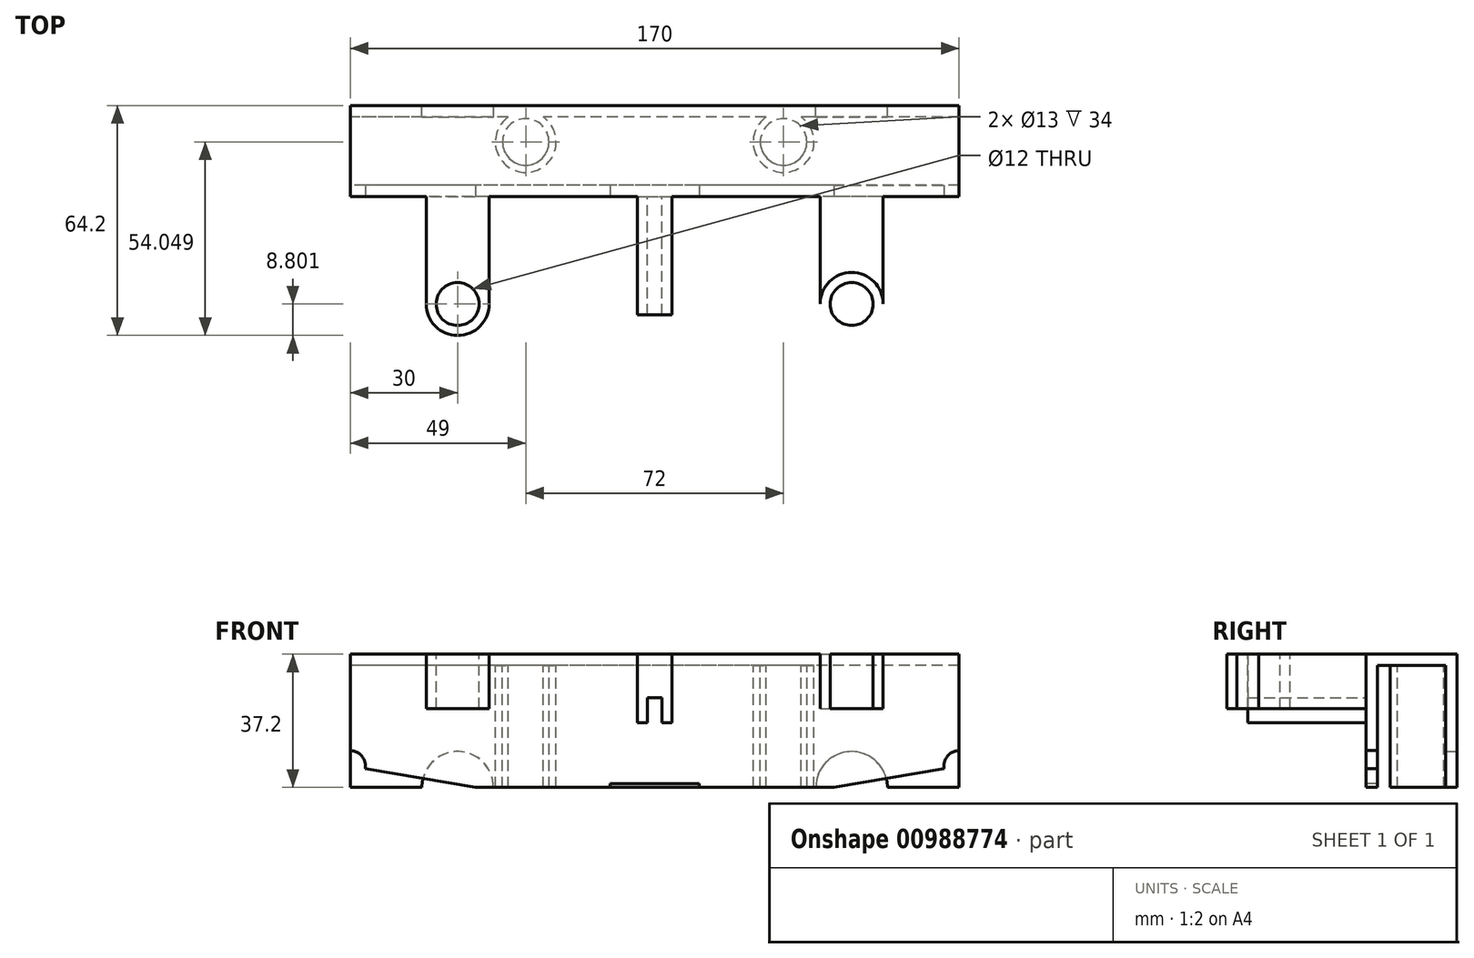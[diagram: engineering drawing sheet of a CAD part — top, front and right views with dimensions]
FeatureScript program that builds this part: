
annotation { "Feature Type Name" : "Feature", "Feature Type Description" : "" }
export const myFeature = defineFeature(function(context is Context, id is Id, definition is map)
    precondition{}
    {
        {
            var Q0;
            Q0=qCreatedBy(makeId("Right.planeOp"),FACE);
            var sketch = newSketch(context, id + "F0", { "sketchPlane" : qUnion([Q0])});
            skLineSegment(sketch, "E0", {"start": v(2.75, 37.2) * mm, "end": v(-22.65, 37.2) * mm});
            skLineSegment(sketch, "E1", {"start": v(-22.65, 37.2) * mm, "end": v(-22.65, 0) * mm});
            skLineSegment(sketch, "E2", {"start": v(-22.65, 0) * mm, "end": v(-19.45, 0) * mm});
            skLineSegment(sketch, "E3", {"start": v(-19.45, 0) * mm, "end": v(-19.45, 34) * mm});
            skLineSegment(sketch, "E4", {"start": v(-19.45, 34) * mm, "end": v(-0.45, 34) * mm});
            skLineSegment(sketch, "E5", {"start": v(-0.45, 34) * mm, "end": v(-0.45, 0) * mm});
            skLineSegment(sketch, "E6", {"start": v(-0.45, 0) * mm, "end": v(2.75, 0) * mm});
            skLineSegment(sketch, "E7", {"start": v(2.75, 0) * mm, "end": v(2.75, 37.2) * mm});
            skSolve(sketch);
        }
        {
            var Q0;
            Q0=makeQuery(id+"F0.imprint","IMPRINT",FACE,{"disambiguationData":[TD([[makeQuery(id+"F0.imprint","IMPRINT",EDGE,{"derivedFrom":sQuery(id+"F0.wireOp",EDGE,"E0")}),1.0]])]});
            extrude(context, id + "F1", {"entities" : qUnion([Q0]), "endBound" : BoundingType.SYMMETRIC, "depth" : 170 * mm, "offsetDistance" : 25 * mm});
        }
        {
            var Q0;
            Q0=makeQuery(id+"F1.opExtrude","SWEPT_FACE",FACE,{"disambiguationData":[OSD([sQuery(id+"F0.wireOp",EDGE,"E7")])]});
            var sketch = newSketch(context, id + "F2", { "sketchPlane" : qUnion([Q0])});
            skLineSegment(sketch, "E8", {"start": v(-55, 0) * mm, "end": v(55, 0) * mm, "construction": true});
            skPoint(sketch, "E9", {"position": v(0, 0) * mm});
            skArc(sketch, "E10", {"start": v(-45, 0) * mm, "mid": v(-55, 10) * mm, "end": v(-65, 0) * mm});
            skArc(sketch, "E11", {"start": v(65, 0) * mm, "mid": v(55, 10) * mm, "end": v(45, 0) * mm});
            skLineSegment(sketch, "E12", {"start": v(-65, 0) * mm, "end": v(-45, 0) * mm});
            skLineSegment(sketch, "E13", {"start": v(45, 0) * mm, "end": v(65, 0) * mm});
            skSolve(sketch);
        }
        {
            var Q0;
            Q0=makeQuery(id+"F2.imprint","IMPRINT",FACE,{"disambiguationData":[TD([[makeQuery(id+"F2.imprint","IMPRINT",EDGE,{"derivedFrom":sQuery(id+"F2.wireOp",EDGE,"E10")}),1.0]])]});
            var Q1;
            Q1=makeQuery(id+"F2.imprint","IMPRINT",FACE,{"disambiguationData":[TD([[makeQuery(id+"F2.imprint","IMPRINT",EDGE,{"derivedFrom":sQuery(id+"F2.wireOp",EDGE,"E11")}),1.0]])]});
            var Q2;
            Q2=makeQuery(id+"F1.opExtrude","SWEPT_FACE",FACE,{"disambiguationData":[OSD([sQuery(id+"F0.wireOp",EDGE,"E5")])]});
            extrude(context, id + "F3", {"entities" : qUnion([Q0, Q1]), "operationType" : NewBodyOperationType.REMOVE, "endBound" : BoundingType.UP_TO_SURFACE, "oppositeDirection" : true, "depth" : 25 * mm, "endBoundEntityFace" : qUnion([Q2]), "offsetDistance" : 25 * mm});
        }
        {
            var Q0;
            Q0=makeQuery(id+"F1.opExtrude","SWEPT_FACE",FACE,{"disambiguationData":[OSD([sQuery(id+"F0.wireOp",EDGE,"E1")])]});
            var sketch = newSketch(context, id + "F4", { "sketchPlane" : qUnion([Q0])});
            skPoint(sketch, "E14.0", {"position": v(0, 34) * mm});
            skLineSegment(sketch, "E15", {"start": v(-85, 6) * mm, "end": v(-50, 0) * mm});
            skLineSegment(sketch, "E16", {"start": v(-50, 0) * mm, "end": v(-85, 0) * mm});
            skLineSegment(sketch, "E17", {"start": v(-85, 0) * mm, "end": v(-85, 6) * mm});
            skLineSegment(sketch, "E18.MirrorCS", {"start": v(85, 6) * mm, "end": v(50, 0) * mm});
            skLineSegment(sketch, "E19.MirrorCS", {"start": v(50, 0) * mm, "end": v(85, 0) * mm});
            skLineSegment(sketch, "E20.MirrorCS", {"start": v(85, 0) * mm, "end": v(85, 6) * mm});
            skLineSegment(sketch, "E21", {"start": v(-12.5, 1) * mm, "end": v(12.5, 1) * mm});
            skPoint(sketch, "E22", {"position": v(0, 1) * mm});
            skLineSegment(sketch, "E23", {"start": v(-12.5, 1) * mm, "end": v(-12.5, 0) * mm});
            skLineSegment(sketch, "E24", {"start": v(-12.5, 0) * mm, "end": v(12.5, 0) * mm});
            skLineSegment(sketch, "E25", {"start": v(12.5, 0) * mm, "end": v(12.5, 1) * mm});
            skLineSegment(sketch, "E26", {"start": v(-82, 9) * mm, "end": v(82, 9) * mm, "construction": true});
            skPoint(sketch, "E27", {"position": v(0, 9) * mm});
            skArc(sketch, "E28", {"start": v(85, 10.24) * mm, "mid": v(81.76, 8.73) * mm, "end": v(80.82, 5.28) * mm});
            skLineSegment(sketch, "E29", {"start": v(85, 6) * mm, "end": v(85, 10.24) * mm});
            skArc(sketch, "E30", {"start": v(-80.82, 5.28) * mm, "mid": v(-81.76, 8.73) * mm, "end": v(-85, 10.24) * mm});
            skLineSegment(sketch, "E31", {"start": v(-85, 10.24) * mm, "end": v(-85, 6) * mm});
            skSolve(sketch);
        }
        {
            var Q0;
            Q0=makeQuery(id+"F4.imprint","IMPRINT",FACE,{"disambiguationData":[TD([[makeQuery(id+"F4.imprint","IMPRINT",EDGE,{"derivedFrom":sQuery(id+"F4.wireOp",EDGE,"E15")}),-1.0]])]});
            var Q1;
            Q1=makeQuery(id+"F4.imprint","IMPRINT",FACE,{"disambiguationData":[TD([[makeQuery(id+"F4.imprint","IMPRINT",EDGE,{"derivedFrom":sQuery(id+"F4.wireOp",EDGE,"E18.MirrorCS")}),1.0]])]});
            var Q2;
            Q2=makeQuery(id+"F4.imprint","IMPRINT",FACE,{"disambiguationData":[TD([[makeQuery(id+"F4.imprint","IMPRINT",EDGE,{"derivedFrom":sQuery(id+"F4.wireOp",EDGE,"E21")}),-1.0]])]});
            var Q3;
            {var subQ2=sQuery(id+"F4.wireOp",EDGE,"E30");Q3=makeQuery(id+"F4.imprint","IMPRINT",FACE,{"disambiguationData":[TD([[makeQuery(id+"F4.imprint","IMPRINT",EDGE,{"derivedFrom":subQ2}),1.0]])]});}
            var Q4;
            {var subQ2=sQuery(id+"F4.wireOp",EDGE,"E28");Q4=makeQuery(id+"F4.imprint","IMPRINT",FACE,{"disambiguationData":[TD([[makeQuery(id+"F4.imprint","IMPRINT",EDGE,{"derivedFrom":subQ2}),1.0]])]});}
            var Q5;
            Q5=makeQuery(id+"F1.opExtrude","SWEPT_FACE",FACE,{"disambiguationData":[OSD([sQuery(id+"F0.wireOp",EDGE,"E3")])]});
            extrude(context, id + "F5", {"entities" : qUnion([Q0, Q1, Q2, Q3, Q4]), "operationType" : NewBodyOperationType.REMOVE, "endBound" : BoundingType.UP_TO_SURFACE, "oppositeDirection" : true, "depth" : 25 * mm, "endBoundEntityFace" : qUnion([Q5]), "offsetDistance" : 25 * mm});
        }
        {
            var Q0;
            Q0=makeQuery(id+"F1.opExtrude","SWEPT_FACE",FACE,{"disambiguationData":[OSD([sQuery(id+"F0.wireOp",EDGE,"E4")])]});
            var sketch = newSketch(context, id + "F6", { "sketchPlane" : qUnion([Q0])});
            skLineSegment(sketch, "E32", {"start": v(-36, 7.4) * mm, "end": v(36, 7.4) * mm, "construction": true});
            skPoint(sketch, "E33", {"position": v(0, 7.4) * mm});
            skCircle(sketch, "E34", {"center": v(-36, 7.4) * mm, "radius": 6.5 * mm});
            skCircle(sketch, "E35", {"center": v(36, 7.4) * mm, "radius": 6.5 * mm});
            skArc(sketch, "E36.0", {"start": v(-31.1, 0.45) * mm, "mid": v(-36, 15.9) * mm, "end": v(-40.9, 0.45) * mm});
            skArc(sketch, "E37.0", {"start": v(40.9, 0.45) * mm, "mid": v(36, 15.9) * mm, "end": v(31.1, 0.45) * mm});
            skLineSegment(sketch, "E38", {"start": v(-40.9, 0.45) * mm, "end": v(-31.1, 0.45) * mm});
            skLineSegment(sketch, "E39", {"start": v(31.1, 0.45) * mm, "end": v(40.9, 0.45) * mm});
            skSolve(sketch);
        }
        {
            var Q0;
            Q0=makeQuery(id+"F6.imprint","IMPRINT",FACE,{"disambiguationData":[TD([[makeQuery(id+"F6.imprint","IMPRINT",EDGE,{"derivedFrom":sQuery(id+"F6.wireOp",EDGE,"E35")}),-1.0]])]});
            var Q1;
            Q1=makeQuery(id+"F6.imprint","IMPRINT",FACE,{"disambiguationData":[TD([[makeQuery(id+"F6.imprint","IMPRINT",EDGE,{"derivedFrom":sQuery(id+"F6.wireOp",EDGE,"E34")}),-1.0]])]});
            var Q2;
            Q2=makeQuery(id+"F3.boolean.opBoolean","SPLIT",FACE,{"disambiguationData":[TD([makeQuery(id+"F1.opExtrude","SWEPT_FACE",FACE,{"disambiguationData":[OSD([sQuery(id+"F0.wireOp",EDGE,"E5")])]}),makeQuery(id+"F1.opExtrude","SWEPT_FACE",FACE,{"disambiguationData":[OSD([sQuery(id+"F0.wireOp",EDGE,"E7")])]}),makeQuery(id+"F3.opExtrude","SWEPT_FACE",FACE,{"disambiguationData":[OSD([sQuery(id+"F2.wireOp",EDGE,"E10")])]}),makeQuery(id+"F3.opExtrude","SWEPT_FACE",FACE,{"disambiguationData":[OSD([sQuery(id+"F2.wireOp",EDGE,"E11")])]})])],"derivedFrom":makeQuery(id+"F1.opExtrude","SWEPT_FACE",FACE,{"disambiguationData":[OSD([sQuery(id+"F0.wireOp",EDGE,"E6")])]})});
            extrude(context, id + "F7", {"entities" : qUnion([Q0, Q1]), "operationType" : NewBodyOperationType.ADD, "endBound" : BoundingType.UP_TO_SURFACE, "depth" : 25 * mm, "endBoundEntityFace" : qUnion([Q2]), "offsetDistance" : 25 * mm});
        }
        {
            var Q0;
            Q0=makeQuery(id+"F1.opExtrude","SWEPT_FACE",FACE,{"disambiguationData":[OSD([sQuery(id+"F0.wireOp",EDGE,"E1")])]});
            var sketch = newSketch(context, id + "F8", { "sketchPlane" : qUnion([Q0])});
            skPoint(sketch, "E40", {"position": v(0, 25) * mm});
            skLineSegment(sketch, "E41", {"start": v(-2, 25) * mm, "end": v(2, 25) * mm});
            skLineSegment(sketch, "E42", {"start": v(-2, 25) * mm, "end": v(-2, 18) * mm});
            skLineSegment(sketch, "E43", {"start": v(2, 18) * mm, "end": v(2, 25) * mm});
            skLineSegment(sketch, "E44", {"start": v(2, 18) * mm, "end": v(4.8, 18) * mm});
            skLineSegment(sketch, "E45", {"start": v(4.8, 18) * mm, "end": v(4.8, 27.8) * mm});
            skLineSegment(sketch, "E46", {"start": v(4.8, 27.8) * mm, "end": v(-4.8, 27.8) * mm});
            skLineSegment(sketch, "E47", {"start": v(-4.8, 27.8) * mm, "end": v(-4.8, 18) * mm});
            skLineSegment(sketch, "E48", {"start": v(-4.8, 18) * mm, "end": v(-2, 18) * mm});
            skSolve(sketch);
        }
        {
            var Q0;
            Q0=makeQuery(id+"F8.imprint","IMPRINT",FACE,{"disambiguationData":[TD([[makeQuery(id+"F8.imprint","IMPRINT",EDGE,{"derivedFrom":sQuery(id+"F8.wireOp",EDGE,"E41")}),1.0]])]});
            extrude(context, id + "F9", {"entities" : qUnion([Q0]), "operationType" : NewBodyOperationType.ADD, "depth" : 33 * mm, "offsetDistance" : 25 * mm});
        }
        {
            var Q0;
            Q0=makeQuery(id+"F5.boolean.opBoolean","SPLIT",FACE,{"disambiguationData":[TD([makeQuery(id+"F5.opExtrude","SWEPT_FACE",FACE,{"disambiguationData":[OSD([sQuery(id+"F4.wireOp",EDGE,"E15")])]})])],"derivedFrom":makeQuery(id+"F1.opExtrude","SWEPT_FACE",FACE,{"disambiguationData":[OSD([sQuery(id+"F0.wireOp",EDGE,"E2")])]})});
            cPlane(context, id + "F10", {"entities" : qUnion([Q0]), "cplaneType" : CPlaneType.OFFSET, "offset" : 27 * mm, "oppositeDirection" : true, "width" : 150 * mm, "height" : 150 * mm});
        }
        {
            var Q0;
            Q0=qCreatedBy(id+"F10.planeOp",FACE);
            var sketch = newSketch(context, id + "F11", { "sketchPlane" : qUnion([Q0])});
            skPoint(sketch, "E49.0", {"position": v(-55, 52.65) * mm});
            skCircle(sketch, "E50", {"center": v(-55, 52.65) * mm, "radius": 6 * mm});
            skLineSegment(sketch, "E51.0", {"start": v(85, 22.65) * mm, "end": v(-85, 22.65) * mm, "construction": true});
            skCircle(sketch, "E52.0", {"center": v(-55, 52.65) * mm, "radius": 8.8 * mm});
            skLineSegment(sketch, "E53", {"start": v(-46.2, 52.65) * mm, "end": v(-46.2, 22.65) * mm});
            skLineSegment(sketch, "E54", {"start": v(-46.2, 22.65) * mm, "end": v(-63.8, 22.65) * mm});
            skLineSegment(sketch, "E55", {"start": v(-63.8, 22.65) * mm, "end": v(-63.8, 52.65) * mm});
            skCircle(sketch, "E56.MirrorC", {"center": v(55, 52.65) * mm, "radius": 8.8 * mm});
            skCircle(sketch, "E57.MirrorC", {"center": v(55, 52.65) * mm, "radius": 6 * mm});
            skLineSegment(sketch, "E58.MirrorCS", {"start": v(46.2, 52.65) * mm, "end": v(46.2, 22.65) * mm});
            skLineSegment(sketch, "E59.MirrorCS", {"start": v(63.8, 22.65) * mm, "end": v(63.8, 52.65) * mm});
            skLineSegment(sketch, "E60", {"start": v(63.8, 22.65) * mm, "end": v(46.2, 22.65) * mm});
            skSolve(sketch);
        }
        {
            var Q0;
            {var subQ0=sQuery(id+"F11.wireOp",EDGE,"E53");Q0=makeQuery(id+"F11.imprint","IMPRINT",FACE,{"disambiguationData":[TD([[makeQuery(id+"F11.imprint","IMPRINT",EDGE,{"derivedFrom":subQ0}),-1.0]])]});}
            var Q1;
            Q1=makeQuery(id+"F11.imprint","IMPRINT",FACE,{"disambiguationData":[TD([[makeQuery(id+"F11.imprint","IMPRINT",EDGE,{"derivedFrom":sQuery(id+"F11.wireOp",EDGE,"E50")}),-1.0]])]});
            var Q2;
            {var subQ0=sQuery(id+"F11.wireOp",EDGE,"E58.MirrorCS");Q2=makeQuery(id+"F11.imprint","IMPRINT",FACE,{"disambiguationData":[TD([[makeQuery(id+"F11.imprint","IMPRINT",EDGE,{"derivedFrom":subQ0}),1.0]])]});}
            var Q3;
            Q3=makeQuery(id+"F11.imprint","IMPRINT",FACE,{"disambiguationData":[TD([[makeQuery(id+"F11.imprint","IMPRINT",EDGE,{"derivedFrom":sQuery(id+"F11.wireOp",EDGE,"E57.MirrorC")}),1.0]])]});
            var Q4;
            Q4=makeQuery(id+"F1.opExtrude","SWEPT_FACE",FACE,{"disambiguationData":[OSD([sQuery(id+"F0.wireOp",EDGE,"E0")])]});
            extrude(context, id + "F12", {"entities" : qUnion([Q0, Q1, Q2, Q3]), "operationType" : NewBodyOperationType.ADD, "depth" : 5 * mm, "offsetDistance" : 25 * mm, "hasSecondDirection" : true, "secondDirectionBound" : SecondDirectionBoundingType.UP_TO_SURFACE, "secondDirectionOppositeDirection" : true, "secondDirectionDepth" : 25 * mm, "secondDirectionBoundEntityFace" : qUnion([Q4])});
        }
        {
            var Q0;
            Q0=makeQuery(id+"F9.opExtrude","SWEPT_FACE",FACE,{"disambiguationData":[OSD([sQuery(id+"F8.wireOp",EDGE,"E46")])]});
            var Q1;
            Q1=makeQuery(id+"F12.boolean.opBoolean","MERGE",FACE,{"derivedFrom":[makeQuery(id+"F1.opExtrude","SWEPT_FACE",FACE,{"disambiguationData":[OSD([sQuery(id+"F0.wireOp",EDGE,"E0")])]}),makeQuery(id+"F12.opExtrude","CAP_FACE",FACE,{"disambiguationData":[OSD([sQuery(id+"F11.wireOp",EDGE,"E50"),sQuery(id+"F11.wireOp",EDGE,"E52.0"),sQuery(id+"F11.wireOp",EDGE,"E53"),sQuery(id+"F11.wireOp",EDGE,"E54"),sQuery(id+"F11.wireOp",EDGE,"E55")])],"isStart":true}),makeQuery(id+"F12.opExtrude","CAP_FACE",FACE,{"disambiguationData":[OSD([sQuery(id+"F11.wireOp",EDGE,"E56.MirrorC"),sQuery(id+"F11.wireOp",EDGE,"E57.MirrorC"),sQuery(id+"F11.wireOp",EDGE,"E58.MirrorCS"),sQuery(id+"F11.wireOp",EDGE,"E59.MirrorCS"),sQuery(id+"F11.wireOp",EDGE,"E60")])],"isStart":true})]});
            extrude(context, id + "F13", {"entities" : qUnion([Q0]), "operationType" : NewBodyOperationType.ADD, "endBound" : BoundingType.UP_TO_SURFACE, "depth" : 25 * mm, "endBoundEntityFace" : qUnion([Q1]), "offsetDistance" : 25 * mm});
        }
    });
